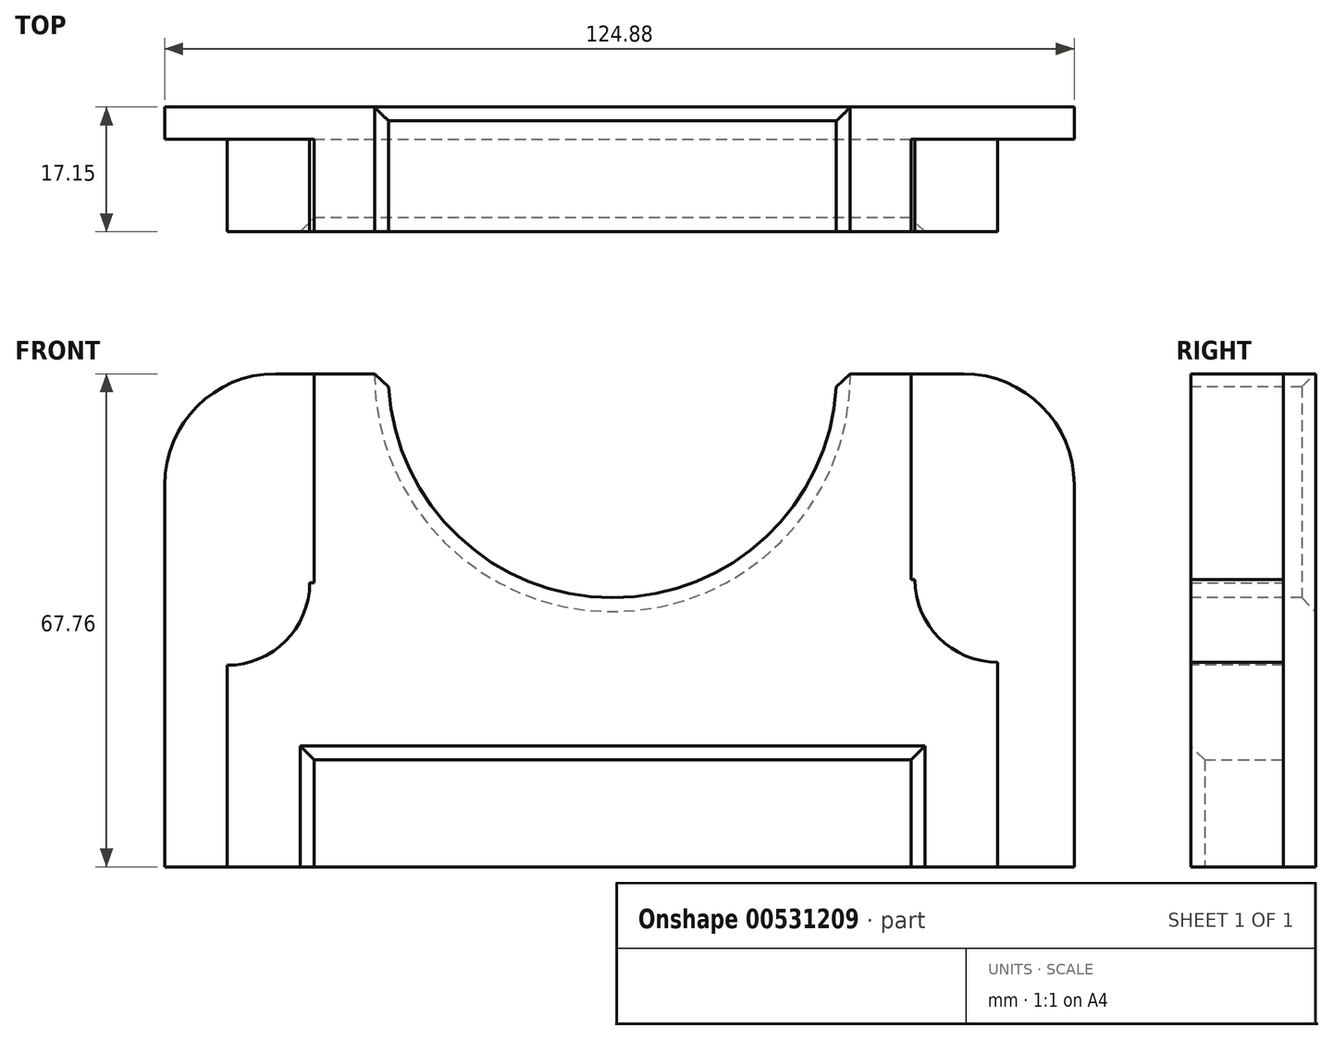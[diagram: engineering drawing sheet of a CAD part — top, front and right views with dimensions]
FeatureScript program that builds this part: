
annotation { "Feature Type Name" : "Feature", "Feature Type Description" : "" }
export const myFeature = defineFeature(function(context is Context, id is Id, definition is map)
    precondition{}
    {
        {
            var Q0;
            Q0=qCreatedBy(makeId("Front.planeOp"),FACE);
            var sketch = newSketch(context, id + "F0", { "sketchPlane" : qUnion([Q0])});
            skLineSegment(sketch, "E0.bottom", {"start": v(-61.5, 0) * mm, "end": v(63.4, 0) * mm});
            skLineSegment(sketch, "E0.top", {"start": v(-61.5, 67.76) * mm, "end": v(63.4, 67.76) * mm});
            skLineSegment(sketch, "E0.left", {"start": v(-61.5, 0) * mm, "end": v(-61.5, 67.76) * mm});
            skLineSegment(sketch, "E0.right", {"start": v(63.4, 0) * mm, "end": v(63.4, 67.76) * mm});
            skSolve(sketch);
        }
        {
            var Q0;
            Q0 = qSketchRegion(id + "F0", true);
            extrude(context, id + "F1", {"entities" : qUnion([Q0]), "depth" : 4.44 * mm, "offsetDistance" : 25.4 * mm});
        }
        {
            var Q0;
            Q0=makeQuery(id+"F1.opExtrude","SWEPT_EDGE",EDGE,{"disambiguationData":[OSD([sQuery(id+"F0.wireOp",EDGE,"E0.top"),sQuery(id+"F0.wireOp",EDGE,"E0.left")])]});
            var Q1;
            Q1=makeQuery(id+"F1.opExtrude","SWEPT_EDGE",EDGE,{"disambiguationData":[OSD([sQuery(id+"F0.wireOp",EDGE,"E0.top"),sQuery(id+"F0.wireOp",EDGE,"E0.right")])]});
            fillet(context, id + "F2", {"entities" : qUnion([Q0, Q1]), "radius" : 15.24 * mm, "tangentPropagation" : true, "allowEdgeOverflow" : false});
        }
        {
            var Q0;
            Q0=makeQuery(id+"F1.opExtrude","CAP_FACE",FACE,{"disambiguationData":[OSD([sQuery(id+"F0.wireOp",EDGE,"E0.bottom"),sQuery(id+"F0.wireOp",EDGE,"E0.top"),sQuery(id+"F0.wireOp",EDGE,"E0.left"),sQuery(id+"F0.wireOp",EDGE,"E0.right")])],"isStart":false});
            var sketch = newSketch(context, id + "F3", { "sketchPlane" : qUnion([Q0])});
            skLineSegment(sketch, "E1.bottom", {"start": v(-41, 67.76) * mm, "end": v(41, 67.76) * mm});
            skLineSegment(sketch, "E1.top", {"start": v(-41, 14.7) * mm, "end": v(41, 14.7) * mm});
            skLineSegment(sketch, "E1.left", {"start": v(-41, 67.76) * mm, "end": v(-41, 14.7) * mm});
            skLineSegment(sketch, "E1.right", {"start": v(41, 67.76) * mm, "end": v(41, 14.7) * mm});
            skLineSegment(sketch, "E2.bottom", {"start": v(41, 39.48) * mm, "end": v(52.88, 39.48) * mm});
            skLineSegment(sketch, "E2.top", {"start": v(41, 0) * mm, "end": v(52.88, 0) * mm});
            skLineSegment(sketch, "E2.left", {"start": v(41, 39.48) * mm, "end": v(41, 0) * mm});
            skLineSegment(sketch, "E2.right", {"start": v(52.88, 39.48) * mm, "end": v(52.88, 0) * mm});
            skLineSegment(sketch, "E3.bottom", {"start": v(-41, 39.06) * mm, "end": v(-52.94, 39.06) * mm});
            skLineSegment(sketch, "E3.top", {"start": v(-41, 0) * mm, "end": v(-52.94, 0) * mm});
            skLineSegment(sketch, "E3.left", {"start": v(-41, 39.06) * mm, "end": v(-41, 0) * mm});
            skLineSegment(sketch, "E3.right", {"start": v(-52.94, 39.06) * mm, "end": v(-52.94, 0) * mm});
            skSolve(sketch);
        }
        {
            var Q0;
            Q0=makeQuery(id+"F3.imprint","IMPRINT",FACE,{"disambiguationData":[TD([[makeQuery(id+"F3.imprint","IMPRINT",EDGE,{"derivedFrom":sQuery(id+"F3.wireOp",EDGE,"E1.bottom")}),-1.0]])]});
            var Q1;
            {var subQ3=sQuery(id+"F3.wireOp",EDGE,"E3.bottom");Q1=makeQuery(id+"F3.imprint","IMPRINT",FACE,{"disambiguationData":[TD([[makeQuery(id+"F3.imprint","IMPRINT",EDGE,{"derivedFrom":subQ3}),1.0]])]});}
            var Q2;
            {var subQ3=sQuery(id+"F3.wireOp",EDGE,"E2.bottom");Q2=makeQuery(id+"F3.imprint","IMPRINT",FACE,{"disambiguationData":[TD([[makeQuery(id+"F3.imprint","IMPRINT",EDGE,{"derivedFrom":subQ3}),-1.0]])]});}
            extrude(context, id + "F4", {"entities" : qUnion([Q0, Q1, Q2]), "operationType" : NewBodyOperationType.ADD, "depth" : 12.7 * mm, "offsetDistance" : 25.4 * mm});
        }
        {
            var Q0;
            Q0=makeQuery(id+"F4.opExtrude","CAP_FACE",FACE,{"disambiguationData":[OSD([sQuery(id+"F3.wireOp",EDGE,"E1.bottom"),sQuery(id+"F3.wireOp",EDGE,"E1.top"),sQuery(id+"F3.wireOp",EDGE,"E1.left"),sQuery(id+"F3.wireOp",EDGE,"E1.right"),sQuery(id+"F3.wireOp",EDGE,"E2.bottom"),sQuery(id+"F3.wireOp",EDGE,"E2.top"),sQuery(id+"F3.wireOp",EDGE,"E2.left"),sQuery(id+"F3.wireOp",EDGE,"E2.right"),sQuery(id+"F3.wireOp",EDGE,"E3.bottom"),sQuery(id+"F3.wireOp",EDGE,"E3.top"),sQuery(id+"F3.wireOp",EDGE,"E3.left"),sQuery(id+"F3.wireOp",EDGE,"E3.right")])],"isStart":false});
            var sketch = newSketch(context, id + "F5", { "sketchPlane" : qUnion([Q0])});
            skCircle(sketch, "E4", {"center": v(0, 67.76) * mm, "radius": 30.78 * mm});
            skSolve(sketch);
        }
        {
            var Q0;
            {var subQ0=sQuery(id+"F5.wireOp",EDGE,"E4");var subQ1=makeQuery(id+"F4.opExtrude","CAP_EDGE",EDGE,{"disambiguationData":[OSD([sQuery(id+"F3.wireOp",EDGE,"E1.bottom")])],"isStart":false});var subQ2=makeQuery(id+"F5.imprint","INTERSECT",VERTEX,{"disambiguationData":[OD(0.0)],"derivedFrom":[subQ1,subQ0]});Q0=makeQuery(id+"F5.imprint","IMPRINT",FACE,{"disambiguationData":[TD([[makeQuery(id+"F5.imprint","IMPRINT",EDGE,{"disambiguationData":[TD([[subQ2,-1.0]])],"derivedFrom":subQ0}),1.0]])]});}
            var Q1;
            {var subQ0=sQuery(id+"F5.wireOp",EDGE,"E4");var subQ1=makeQuery(id+"F4.opExtrude","CAP_EDGE",EDGE,{"disambiguationData":[OSD([sQuery(id+"F3.wireOp",EDGE,"E1.bottom")])],"isStart":false});var subQ2=makeQuery(id+"F5.imprint","INTERSECT",VERTEX,{"disambiguationData":[OD(0.0)],"derivedFrom":[subQ1,subQ0]});Q1=makeQuery(id+"F5.imprint","IMPRINT",FACE,{"disambiguationData":[TD([[makeQuery(id+"F5.imprint","IMPRINT",EDGE,{"disambiguationData":[TD([[subQ2,1.0]])],"derivedFrom":subQ0}),1.0]])]});}
            extrude(context, id + "F6", {"entities" : qUnion([Q0, Q1]), "operationType" : NewBodyOperationType.REMOVE, "oppositeDirection" : true, "depth" : 50.8 * mm, "offsetDistance" : 25.4 * mm});
        }
        {
            var Q0;
            Q0=makeQuery(id+"F4.opExtrude","CAP_FACE",FACE,{"disambiguationData":[OSD([sQuery(id+"F3.wireOp",EDGE,"E1.bottom"),sQuery(id+"F3.wireOp",EDGE,"E1.top"),sQuery(id+"F3.wireOp",EDGE,"E1.left"),sQuery(id+"F3.wireOp",EDGE,"E1.right"),sQuery(id+"F3.wireOp",EDGE,"E2.bottom"),sQuery(id+"F3.wireOp",EDGE,"E2.top"),sQuery(id+"F3.wireOp",EDGE,"E2.left"),sQuery(id+"F3.wireOp",EDGE,"E2.right"),sQuery(id+"F3.wireOp",EDGE,"E3.bottom"),sQuery(id+"F3.wireOp",EDGE,"E3.top"),sQuery(id+"F3.wireOp",EDGE,"E3.left"),sQuery(id+"F3.wireOp",EDGE,"E3.right")])],"isStart":false});
            var sketch = newSketch(context, id + "F7", { "sketchPlane" : qUnion([Q0])});
            skCircle(sketch, "E5", {"center": v(52.88, 39.48) * mm, "radius": 11.36 * mm});
            skCircle(sketch, "E6", {"center": v(-52.94, 39.06) * mm, "radius": 11.36 * mm});
            skSolve(sketch);
        }
        {
            var Q0;
            {var subQ0=sQuery(id+"F7.wireOp",EDGE,"E6");var subQ1=makeQuery(id+"F4.opExtrude","CAP_EDGE",EDGE,{"disambiguationData":[OSD([sQuery(id+"F3.wireOp",EDGE,"E3.bottom")])],"isStart":false});var subQ2=makeQuery(id+"F7.imprint","INTERSECT",VERTEX,{"derivedFrom":[subQ1,subQ0]});Q0=makeQuery(id+"F7.imprint","IMPRINT",FACE,{"disambiguationData":[TD([[makeQuery(id+"F7.imprint","IMPRINT",EDGE,{"disambiguationData":[TD([[subQ2,1.0]])],"derivedFrom":subQ0}),1.0]])]});}
            var Q1;
            {var subQ0=sQuery(id+"F7.wireOp",EDGE,"E5");var subQ1=makeQuery(id+"F4.opExtrude","CAP_EDGE",EDGE,{"disambiguationData":[OSD([sQuery(id+"F3.wireOp",EDGE,"E2.bottom")])],"isStart":false});var subQ2=makeQuery(id+"F7.imprint","INTERSECT",VERTEX,{"derivedFrom":[subQ1,subQ0]});Q1=makeQuery(id+"F7.imprint","IMPRINT",FACE,{"disambiguationData":[TD([[makeQuery(id+"F7.imprint","IMPRINT",EDGE,{"disambiguationData":[TD([[subQ2,-1.0]])],"derivedFrom":subQ0}),1.0]])]});}
            extrude(context, id + "F8", {"entities" : qUnion([Q0, Q1]), "operationType" : NewBodyOperationType.REMOVE, "oppositeDirection" : true, "depth" : 12.7 * mm, "offsetDistance" : 25.4 * mm});
        }
        {
            var Q0;
            Q0=makeQuery(id+"F6.boolean.opBoolean","COPY",EDGE,{"derivedFrom":makeQuery(id+"F6.opExtrude","CAP_EDGE",EDGE,{"disambiguationData":[OSD([sQuery(id+"F5.wireOp",EDGE,"E4")])],"isStart":true})});
            var Q1;
            Q1=makeQuery(id+"F6.boolean.opBoolean","INTERSECT",EDGE,{"derivedFrom":[makeQuery(id+"F1.opExtrude","CAP_FACE",FACE,{"disambiguationData":[OSD([sQuery(id+"F0.wireOp",EDGE,"E0.bottom"),sQuery(id+"F0.wireOp",EDGE,"E0.top"),sQuery(id+"F0.wireOp",EDGE,"E0.left"),sQuery(id+"F0.wireOp",EDGE,"E0.right")])],"isStart":true}),makeQuery(id+"F6.opExtrude","SWEPT_FACE",FACE,{"disambiguationData":[OSD([sQuery(id+"F5.wireOp",EDGE,"E4")])]})]});
            var Q2;
            Q2=makeQuery(id+"F6.boolean.opBoolean","INTERSECT",EDGE,{"disambiguationData":[OD(0.0)],"derivedFrom":[makeQuery(id+"F4.boolean.opBoolean","MERGE",FACE,{"derivedFrom":[makeQuery(id+"F1.opExtrude","SWEPT_FACE",FACE,{"disambiguationData":[OSD([sQuery(id+"F0.wireOp",EDGE,"E0.top")])]}),makeQuery(id+"F4.opExtrude","SWEPT_FACE",FACE,{"disambiguationData":[OSD([sQuery(id+"F3.wireOp",EDGE,"E1.bottom")])]})]}),makeQuery(id+"F6.opExtrude","SWEPT_FACE",FACE,{"disambiguationData":[OSD([sQuery(id+"F5.wireOp",EDGE,"E4")])]})]});
            var Q3;
            Q3=makeQuery(id+"F6.boolean.opBoolean","INTERSECT",EDGE,{"disambiguationData":[OD(1.0)],"derivedFrom":[makeQuery(id+"F4.boolean.opBoolean","MERGE",FACE,{"derivedFrom":[makeQuery(id+"F1.opExtrude","SWEPT_FACE",FACE,{"disambiguationData":[OSD([sQuery(id+"F0.wireOp",EDGE,"E0.top")])]}),makeQuery(id+"F4.opExtrude","SWEPT_FACE",FACE,{"disambiguationData":[OSD([sQuery(id+"F3.wireOp",EDGE,"E1.bottom")])]})]}),makeQuery(id+"F6.opExtrude","SWEPT_FACE",FACE,{"disambiguationData":[OSD([sQuery(id+"F5.wireOp",EDGE,"E4")])]})]});
            var Q4;
            Q4=makeQuery(id+"F4.opExtrude","CAP_EDGE",EDGE,{"disambiguationData":[OSD([sQuery(id+"F3.wireOp",EDGE,"E3.left")])],"isStart":false});
            var Q5;
            Q5=makeQuery(id+"F4.opExtrude","CAP_EDGE",EDGE,{"disambiguationData":[OSD([sQuery(id+"F3.wireOp",EDGE,"E2.left")])],"isStart":false});
            var Q6;
            Q6=makeQuery(id+"F4.opExtrude","CAP_EDGE",EDGE,{"disambiguationData":[OSD([sQuery(id+"F3.wireOp",EDGE,"E1.top")])],"isStart":false});
            var Q7;
            Q7=makeQuery(id+"F8.boolean.opBoolean","COPY",EDGE,{"derivedFrom":makeQuery(id+"F8.opExtrude","SWEPT_EDGE",EDGE,{"disambiguationData":[OSD([sQuery(id+"F3.wireOp",EDGE,"E2.right"),sQuery(id+"F7.wireOp",EDGE,"E5")])]})});
            var Q8;
            Q8=makeQuery(id+"F8.boolean.opBoolean","COPY",EDGE,{"derivedFrom":makeQuery(id+"F8.opExtrude","SWEPT_EDGE",EDGE,{"disambiguationData":[OSD([sQuery(id+"F3.wireOp",EDGE,"E3.right"),sQuery(id+"F7.wireOp",EDGE,"E6")])]})});
            var Q9;
            Q9=makeQuery(id+"F8.boolean.opBoolean","COPY",EDGE,{"derivedFrom":makeQuery(id+"F8.opExtrude","SWEPT_EDGE",EDGE,{"disambiguationData":[OSD([sQuery(id+"F3.wireOp",EDGE,"E2.bottom"),sQuery(id+"F7.wireOp",EDGE,"E5")])]})});
            var Q10;
            Q10=makeQuery(id+"F8.boolean.opBoolean","COPY",EDGE,{"derivedFrom":makeQuery(id+"F8.opExtrude","SWEPT_EDGE",EDGE,{"disambiguationData":[OSD([sQuery(id+"F3.wireOp",EDGE,"E3.bottom"),sQuery(id+"F7.wireOp",EDGE,"E6")])]})});
            chamfer(context, id + "F9", {"entities" : qUnion([Q0, Q1, Q2, Q3, Q4, Q5, Q6, Q7, Q8, Q9, Q10]), "width" : 1.9 * mm, "tangentPropagation" : true});
        }
    });
